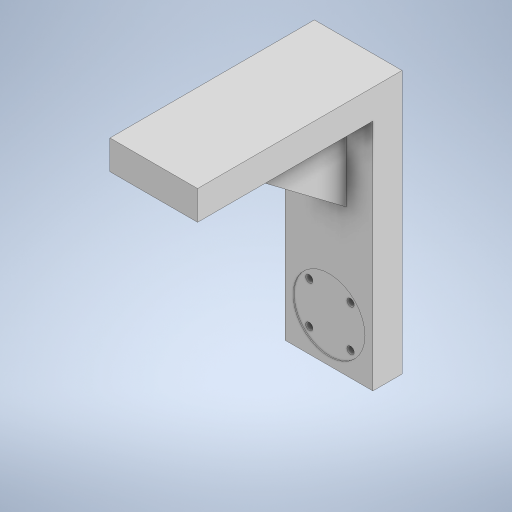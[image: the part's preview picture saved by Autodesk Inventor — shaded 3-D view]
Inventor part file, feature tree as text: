
AUTODESK INVENTOR PART (.ipt)
format: ipt  version: 2024 (Build 280153000, 153)  size: 281,600 bytes
history: native  units: in
note: dims shown in document units (in); Inventor stores cm internally (conversion verified against a paired STEP export)
features: sketch x7, extrude x6, rib x1
ambient origin geometry x8: Origin, YZ Plane, XZ Plane, XY Plane, X Axis, Y Axis, Z Axis, Center Point
bodies: Body1 (feature_tree)
feature tree (14):
  extrude  "Extrusion8"  Depth=1.9685in TaperAngle=0.0deg
  extrude  "Extrusion10"  Depth=3.0in
  extrude  "Extrusion11"  Depth=6.0in TaperAngle=0.0deg
  extrude  "Extrusion12"  Depth=6.0in TaperAngle=0.0deg
  rib  "Rib2"
  extrude  "Extrusion14"  [1 undecoded]
  extrude  "Extrusion15"  Depth=1.0in
  sketch  "Sketch7"  dims[d33=2.463in d34=1.9685in d35=0.0in]
  sketch  "Sketch9"  dims[d43=3.0in d44=3.0in]
  sketch  "Sketch10"  dims[d45=1.0in d46=0.0in d47=6.0in d48=0.0in]
  sketch  "Sketch11"  dims[d49=1.0in d50=6.0in d51=0.0in]
  sketch  "Sketch14"  dims[d70=3.0in d71=-0.3642in]
  sketch  "Sketch16"  dims[d72=4.0in]
  sketch  "Sketch17"  dims[d73=0.0394in d74=1.1811in d75=0.0in d76=0.0in d77=0.0394in d78=0.0394in d89=0.25in d90=0.707in d91=0.707in d92=1.5748in d94=360.0deg d96=1.0in d97=0.0in d98=0.0in d99=2.0in d100=0.0in]
note: 1 required parameter value undecoded (feature->parameter linkage not recoverable at this tier; creation-order binding heuristic only, values carry confidence <= 0.55)
